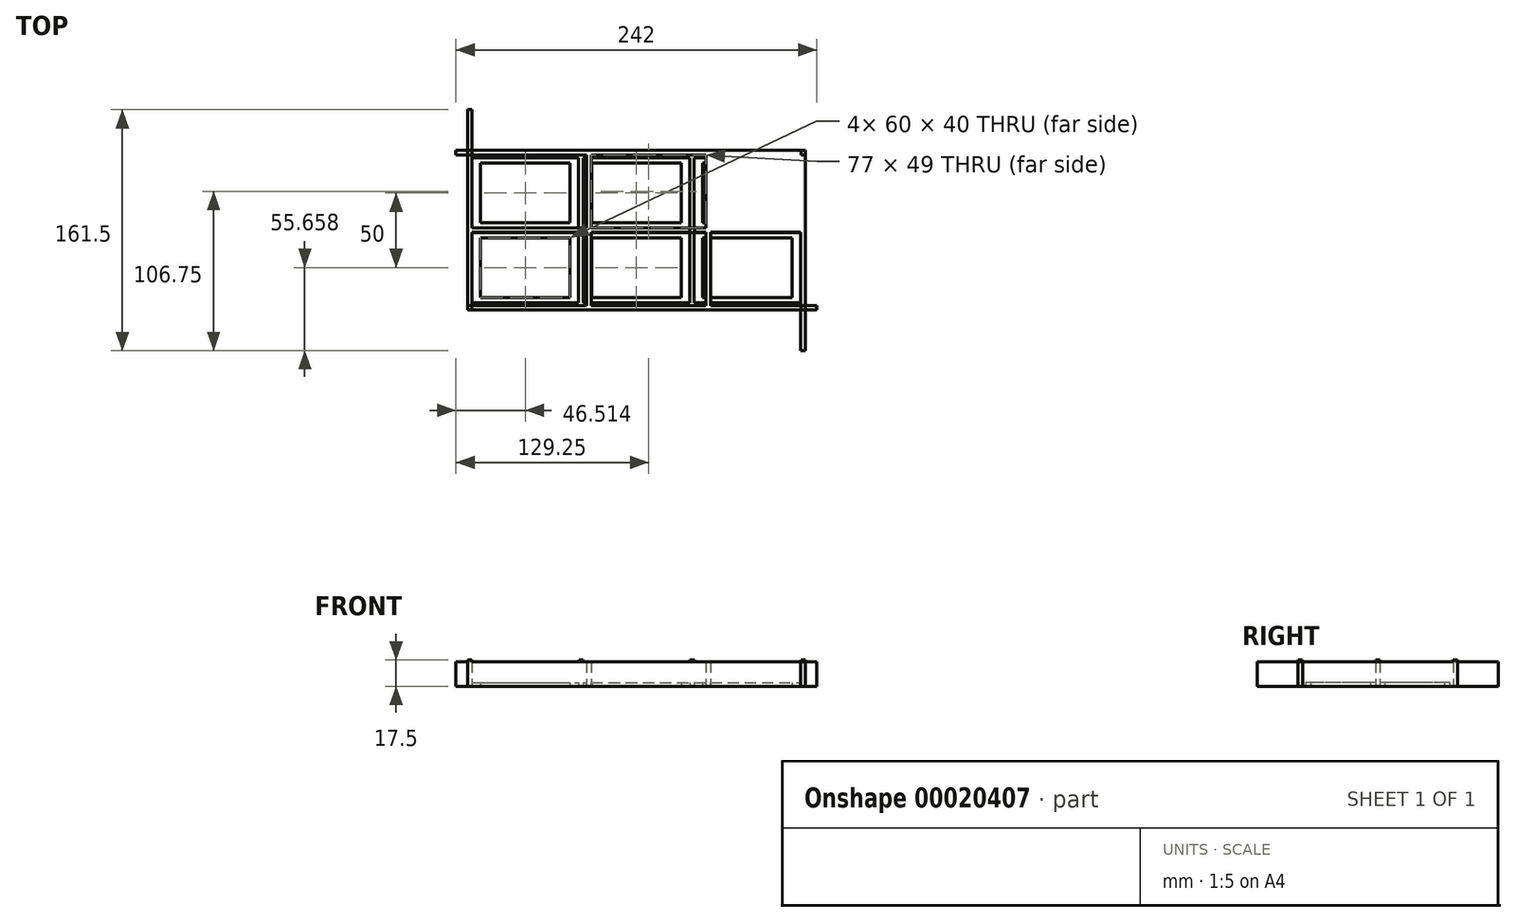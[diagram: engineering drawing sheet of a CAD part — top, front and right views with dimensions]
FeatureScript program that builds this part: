
annotation { "Feature Type Name" : "Feature", "Feature Type Description" : "" }
export const myFeature = defineFeature(function(context is Context, id is Id, definition is map)
    precondition{}
    {
        {
            var Q0;
            Q0=qCreatedBy(makeId("Top.planeOp"),FACE);
            var sketch = newSketch(context, id + "F0", { "sketchPlane" : qUnion([Q0])});
            skLineSegment(sketch, "E0.rect.bottom", {"start": v(113.25, 53.5) * mm, "end": v(-113.25, 53.5) * mm});
            skLineSegment(sketch, "E0.rect.top", {"start": v(113.25, -53.5) * mm, "end": v(-113.25, -53.5) * mm});
            skLineSegment(sketch, "E0.rect.left", {"start": v(113.25, 53.5) * mm, "end": v(113.25, -53.5) * mm});
            skLineSegment(sketch, "E0.rect.right", {"start": v(-113.25, 53.5) * mm, "end": v(-113.25, -53.5) * mm});
            skPoint(sketch, "E0.rect.middle", {"position": v(0, 0) * mm});
            skLineSegment(sketch, "E1.bottom", {"start": v(-110.25, 50.5) * mm, "end": v(-33.25, 50.5) * mm});
            skLineSegment(sketch, "E1.top", {"start": v(-110.25, 1.5) * mm, "end": v(-33.25, 1.5) * mm});
            skLineSegment(sketch, "E1.left", {"start": v(-110.25, 50.5) * mm, "end": v(-110.25, 1.5) * mm});
            skLineSegment(sketch, "E1.right", {"start": v(-33.25, 50.5) * mm, "end": v(-33.25, 1.5) * mm});
            skLineSegment(sketch, "E2.bottom", {"start": v(-110.25, -1.5) * mm, "end": v(-33.25, -1.5) * mm});
            skLineSegment(sketch, "E2.top", {"start": v(-110.25, -50.5) * mm, "end": v(-33.25, -50.5) * mm});
            skLineSegment(sketch, "E2.left", {"start": v(-110.25, -1.5) * mm, "end": v(-110.25, -50.5) * mm});
            skLineSegment(sketch, "E2.right", {"start": v(-33.25, -1.5) * mm, "end": v(-33.25, -50.5) * mm});
            skLineSegment(sketch, "E3.bottom", {"start": v(-30.25, 50.5) * mm, "end": v(46.75, 50.5) * mm});
            skLineSegment(sketch, "E3.top", {"start": v(-30.25, 1.5) * mm, "end": v(46.75, 1.5) * mm});
            skLineSegment(sketch, "E3.left", {"start": v(-30.25, 50.5) * mm, "end": v(-30.25, 1.5) * mm});
            skLineSegment(sketch, "E3.right", {"start": v(46.75, 50.5) * mm, "end": v(46.75, 1.5) * mm});
            skLineSegment(sketch, "E4.bottom", {"start": v(-30.25, -1.5) * mm, "end": v(46.75, -1.5) * mm});
            skLineSegment(sketch, "E4.top", {"start": v(-30.25, -50.5) * mm, "end": v(46.75, -50.5) * mm});
            skLineSegment(sketch, "E4.left", {"start": v(-30.25, -1.5) * mm, "end": v(-30.25, -50.5) * mm});
            skLineSegment(sketch, "E4.right", {"start": v(46.75, -1.5) * mm, "end": v(46.75, -50.5) * mm});
            skLineSegment(sketch, "E5.bottom", {"start": v(49.75, -1.5) * mm, "end": v(110.25, -1.5) * mm});
            skLineSegment(sketch, "E5.top", {"start": v(49.75, -50.5) * mm, "end": v(110.25, -50.5) * mm});
            skLineSegment(sketch, "E5.left", {"start": v(49.75, -1.5) * mm, "end": v(49.75, -50.5) * mm});
            skLineSegment(sketch, "E5.right", {"start": v(110.25, -1.5) * mm, "end": v(110.25, -50.5) * mm});
            skLineSegment(sketch, "E6.bottom", {"start": v(113.25, -50.5) * mm, "end": v(121, -50.5) * mm});
            skLineSegment(sketch, "E6.top", {"start": v(113.25, -53.5) * mm, "end": v(121, -53.5) * mm});
            skLineSegment(sketch, "E6.left", {"start": v(113.25, -50.5) * mm, "end": v(113.25, -53.5) * mm});
            skLineSegment(sketch, "E6.right", {"start": v(121, -50.5) * mm, "end": v(121, -53.5) * mm});
            skLineSegment(sketch, "E7.bottom", {"start": v(110.25, -53.5) * mm, "end": v(113.25, -53.5) * mm});
            skLineSegment(sketch, "E7.top", {"start": v(110.25, -80.75) * mm, "end": v(113.25, -80.75) * mm});
            skLineSegment(sketch, "E7.left", {"start": v(110.25, -53.5) * mm, "end": v(110.25, -80.75) * mm});
            skLineSegment(sketch, "E7.right", {"start": v(113.25, -53.5) * mm, "end": v(113.25, -80.75) * mm});
            skLineSegment(sketch, "E8.bottom", {"start": v(-110.25, 53.5) * mm, "end": v(-113.25, 53.5) * mm});
            skLineSegment(sketch, "E8.top", {"start": v(-110.25, 80.75) * mm, "end": v(-113.25, 80.75) * mm});
            skLineSegment(sketch, "E8.left", {"start": v(-110.25, 53.5) * mm, "end": v(-110.25, 80.75) * mm});
            skLineSegment(sketch, "E8.right", {"start": v(-113.25, 53.5) * mm, "end": v(-113.25, 80.75) * mm});
            skLineSegment(sketch, "E9.bottom", {"start": v(-113.25, 50.5) * mm, "end": v(-121, 50.5) * mm});
            skLineSegment(sketch, "E9.top", {"start": v(-113.25, 53.5) * mm, "end": v(-121, 53.5) * mm});
            skLineSegment(sketch, "E9.left", {"start": v(-113.25, 50.5) * mm, "end": v(-113.25, 53.5) * mm});
            skLineSegment(sketch, "E9.right", {"start": v(-121, 50.5) * mm, "end": v(-121, 53.5) * mm});
            skPoint(sketch, "E10.left.start.orphan", {"position": v(49.75, 50.5) * mm});
            skPoint(sketch, "E10.top.start.orphan", {"position": v(49.75, 1.5) * mm});
            skPoint(sketch, "E10.right.end.orphan", {"position": v(110.25, 1.5) * mm});
            skSolve(sketch);
        }
        {
            var Q0;
            Q0=qSketchRegion(id+"F0",true);
            extrude(context, id + "F1", {"entities" : qUnion([Q0]), "depth" : 16.5 * mm});
        }
        {
            var Q0;
            Q0=qCreatedBy(makeId("Top.planeOp"),FACE);
            var sketch = newSketch(context, id + "F2", { "sketchPlane" : qUnion([Q0])});
            skPoint(sketch, "E11.rect.middle", {"position": v(0.01, -0.1) * mm});
            skLineSegment(sketch, "E12.bottom", {"start": v(-110.24, 48.4) * mm, "end": v(-38.74, 48.4) * mm});
            skLineSegment(sketch, "E12.top", {"start": v(-110.24, 1.4) * mm, "end": v(-38.74, 1.4) * mm});
            skLineSegment(sketch, "E12.left", {"start": v(-110.24, 48.4) * mm, "end": v(-110.24, 1.4) * mm});
            skLineSegment(sketch, "E12.right", {"start": v(-38.74, 48.4) * mm, "end": v(-38.74, 1.4) * mm});
            skLineSegment(sketch, "E13.bottom", {"start": v(-110.24, -1.6) * mm, "end": v(-38.74, -1.6) * mm});
            skLineSegment(sketch, "E13.top", {"start": v(-110.24, -48.6) * mm, "end": v(-38.74, -48.6) * mm});
            skLineSegment(sketch, "E13.left", {"start": v(-110.24, -1.6) * mm, "end": v(-110.24, -48.6) * mm});
            skLineSegment(sketch, "E13.right", {"start": v(-38.74, -1.6) * mm, "end": v(-38.74, -48.6) * mm});
            skLineSegment(sketch, "E14.bottom", {"start": v(-35.74, 48.4) * mm, "end": v(35.76, 48.4) * mm});
            skLineSegment(sketch, "E14.top", {"start": v(-35.74, 1.4) * mm, "end": v(35.76, 1.4) * mm});
            skLineSegment(sketch, "E14.left", {"start": v(-35.74, 48.4) * mm, "end": v(-35.74, 1.4) * mm});
            skLineSegment(sketch, "E14.right", {"start": v(35.76, 48.4) * mm, "end": v(35.76, 1.4) * mm});
            skLineSegment(sketch, "E15.bottom", {"start": v(-35.74, -1.6) * mm, "end": v(35.76, -1.6) * mm});
            skLineSegment(sketch, "E15.top", {"start": v(-35.74, -48.6) * mm, "end": v(35.76, -48.6) * mm});
            skLineSegment(sketch, "E15.left", {"start": v(-35.74, -1.6) * mm, "end": v(-35.74, -48.6) * mm});
            skLineSegment(sketch, "E15.right", {"start": v(35.76, -1.6) * mm, "end": v(35.76, -48.6) * mm});
            skLineSegment(sketch, "E16.bottom", {"start": v(38.76, 48.4) * mm, "end": v(110.26, 48.4) * mm});
            skLineSegment(sketch, "E16.top", {"start": v(38.76, 1.4) * mm, "end": v(110.26, 1.4) * mm});
            skLineSegment(sketch, "E16.left", {"start": v(38.76, 48.4) * mm, "end": v(38.76, 1.4) * mm});
            skLineSegment(sketch, "E16.right", {"start": v(110.26, 48.4) * mm, "end": v(110.26, 1.4) * mm});
            skLineSegment(sketch, "E17.bottom", {"start": v(38.76, -1.6) * mm, "end": v(110.26, -1.6) * mm});
            skLineSegment(sketch, "E17.top", {"start": v(38.76, -48.6) * mm, "end": v(110.26, -48.6) * mm});
            skLineSegment(sketch, "E17.left", {"start": v(38.76, -1.6) * mm, "end": v(38.76, -48.6) * mm});
            skLineSegment(sketch, "E17.right", {"start": v(110.26, -1.6) * mm, "end": v(110.26, -48.6) * mm});
            skLineSegment(sketch, "E18.bottom", {"start": v(-104.49, 44.9) * mm, "end": v(-44.49, 44.9) * mm});
            skLineSegment(sketch, "E18.top", {"start": v(-104.49, 4.9) * mm, "end": v(-44.49, 4.9) * mm});
            skLineSegment(sketch, "E18.left", {"start": v(-104.49, 44.9) * mm, "end": v(-104.49, 4.9) * mm});
            skLineSegment(sketch, "E18.right", {"start": v(-44.49, 44.9) * mm, "end": v(-44.49, 4.9) * mm});
            skLineSegment(sketch, "E19.bottom", {"start": v(-104.49, -5.1) * mm, "end": v(-44.49, -5.1) * mm});
            skLineSegment(sketch, "E19.top", {"start": v(-104.49, -45.1) * mm, "end": v(-44.49, -45.1) * mm});
            skLineSegment(sketch, "E19.left", {"start": v(-104.49, -5.1) * mm, "end": v(-104.49, -45.1) * mm});
            skLineSegment(sketch, "E19.right", {"start": v(-44.49, -5.1) * mm, "end": v(-44.49, -45.1) * mm});
            skLineSegment(sketch, "E20.bottom", {"start": v(-29.99, 44.9) * mm, "end": v(30.01, 44.9) * mm});
            skLineSegment(sketch, "E20.top", {"start": v(-29.99, 4.9) * mm, "end": v(30.01, 4.9) * mm});
            skLineSegment(sketch, "E20.left", {"start": v(-29.99, 44.9) * mm, "end": v(-29.99, 4.9) * mm});
            skLineSegment(sketch, "E20.right", {"start": v(30.01, 44.9) * mm, "end": v(30.01, 4.9) * mm});
            skLineSegment(sketch, "E21.bottom", {"start": v(-29.99, -5.1) * mm, "end": v(30.01, -5.1) * mm});
            skLineSegment(sketch, "E21.top", {"start": v(-29.99, -45.1) * mm, "end": v(30.01, -45.1) * mm});
            skLineSegment(sketch, "E21.left", {"start": v(-29.99, -5.1) * mm, "end": v(-29.99, -45.1) * mm});
            skLineSegment(sketch, "E21.right", {"start": v(30.01, -5.1) * mm, "end": v(30.01, -45.1) * mm});
            skLineSegment(sketch, "E22.bottom", {"start": v(44.51, 44.9) * mm, "end": v(104.51, 44.9) * mm});
            skLineSegment(sketch, "E22.top", {"start": v(44.51, 4.9) * mm, "end": v(104.51, 4.9) * mm});
            skLineSegment(sketch, "E22.left", {"start": v(44.51, 44.9) * mm, "end": v(44.51, 4.9) * mm});
            skLineSegment(sketch, "E22.right", {"start": v(104.51, 44.9) * mm, "end": v(104.51, 4.9) * mm});
            skLineSegment(sketch, "E23.bottom", {"start": v(44.51, -5.1) * mm, "end": v(104.51, -5.1) * mm});
            skLineSegment(sketch, "E23.top", {"start": v(44.51, -45.1) * mm, "end": v(104.51, -45.1) * mm});
            skLineSegment(sketch, "E23.left", {"start": v(44.51, -5.1) * mm, "end": v(44.51, -45.1) * mm});
            skLineSegment(sketch, "E23.right", {"start": v(104.51, -5.1) * mm, "end": v(104.51, -45.1) * mm});
            skSolve(sketch);
        }
        {
            var Q0;
            Q0=qSketchRegion(id+"F2",true);
            extrude(context, id + "F3", {"entities" : qUnion([Q0]), "operationType" : NewBodyOperationType.ADD, "depth" : 2.5 * mm});
        }
        {
            var Q0;
            Q0=makeQuery(id+"F1.opExtrude","CAP_FACE",FACE,{"disambiguationData":[OSD([sQuery(id+"F0.wireOp",EDGE,"E0.rect.bottom"),sQuery(id+"F0.wireOp",EDGE,"E0.rect.top"),sQuery(id+"F0.wireOp",EDGE,"E0.rect.left"),sQuery(id+"F0.wireOp",EDGE,"E0.rect.right"),sQuery(id+"F0.wireOp",EDGE,"E1.bottom"),sQuery(id+"F0.wireOp",EDGE,"E1.top"),sQuery(id+"F0.wireOp",EDGE,"E1.left"),sQuery(id+"F0.wireOp",EDGE,"E1.right"),sQuery(id+"F0.wireOp",EDGE,"E2.bottom"),sQuery(id+"F0.wireOp",EDGE,"E2.top"),sQuery(id+"F0.wireOp",EDGE,"E2.left"),sQuery(id+"F0.wireOp",EDGE,"E2.right"),sQuery(id+"F0.wireOp",EDGE,"E3.bottom"),sQuery(id+"F0.wireOp",EDGE,"E3.top"),sQuery(id+"F0.wireOp",EDGE,"E3.left"),sQuery(id+"F0.wireOp",EDGE,"E3.right"),sQuery(id+"F0.wireOp",EDGE,"E4.bottom"),sQuery(id+"F0.wireOp",EDGE,"E4.top"),sQuery(id+"F0.wireOp",EDGE,"E4.left"),sQuery(id+"F0.wireOp",EDGE,"E4.right"),sQuery(id+"F0.wireOp",EDGE,"E10.bottom"),sQuery(id+"F0.wireOp",EDGE,"E10.top"),sQuery(id+"F0.wireOp",EDGE,"E10.left"),sQuery(id+"F0.wireOp",EDGE,"E10.right"),sQuery(id+"F0.wireOp",EDGE,"E5.bottom"),sQuery(id+"F0.wireOp",EDGE,"E5.top"),sQuery(id+"F0.wireOp",EDGE,"E5.left"),sQuery(id+"F0.wireOp",EDGE,"E5.right"),sQuery(id+"F0.wireOp",EDGE,"E6.bottom"),sQuery(id+"F0.wireOp",EDGE,"E6.top"),sQuery(id+"F0.wireOp",EDGE,"E6.right"),sQuery(id+"F0.wireOp",EDGE,"E7.top"),sQuery(id+"F0.wireOp",EDGE,"E7.left"),sQuery(id+"F0.wireOp",EDGE,"E7.right"),sQuery(id+"F0.wireOp",EDGE,"E8.top"),sQuery(id+"F0.wireOp",EDGE,"E8.left"),sQuery(id+"F0.wireOp",EDGE,"E8.right"),sQuery(id+"F0.wireOp",EDGE,"E9.bottom"),sQuery(id+"F0.wireOp",EDGE,"E9.top"),sQuery(id+"F0.wireOp",EDGE,"E9.right")])],"isStart":false});
            var sketch = newSketch(context, id + "F4", { "sketchPlane" : qUnion([Q0])});
            skPoint(sketch, "E24.rect.middle", {"position": v(0.15, -0.13) * mm});
            skLineSegment(sketch, "E25.bottom", {"start": v(-110.1, 50.37) * mm, "end": v(-113.25, 50.37) * mm});
            skLineSegment(sketch, "E25.top", {"start": v(-110.1, 53.5) * mm, "end": v(-113.25, 53.5) * mm});
            skLineSegment(sketch, "E25.left", {"start": v(-110.1, 50.37) * mm, "end": v(-110.1, 53.5) * mm});
            skLineSegment(sketch, "E25.right", {"start": v(-113.25, 50.37) * mm, "end": v(-113.25, 53.5) * mm});
            skLineSegment(sketch, "E26.bottom", {"start": v(-110.1, -50.63) * mm, "end": v(-113.25, -50.63) * mm});
            skLineSegment(sketch, "E26.top", {"start": v(-110.1, -53.5) * mm, "end": v(-113.25, -53.5) * mm});
            skLineSegment(sketch, "E26.left", {"start": v(-110.1, -50.63) * mm, "end": v(-110.1, -53.5) * mm});
            skLineSegment(sketch, "E26.right", {"start": v(-113.25, -50.63) * mm, "end": v(-113.25, -53.5) * mm});
            skLineSegment(sketch, "E27.bottom", {"start": v(-38.6, -1.63) * mm, "end": v(-35.6, -1.63) * mm});
            skLineSegment(sketch, "E27.top", {"start": v(-38.6, 1.37) * mm, "end": v(-35.6, 1.37) * mm});
            skLineSegment(sketch, "E27.left", {"start": v(-38.6, -1.63) * mm, "end": v(-38.6, 1.37) * mm});
            skLineSegment(sketch, "E27.right", {"start": v(-35.6, -1.63) * mm, "end": v(-35.6, 1.37) * mm});
            skLineSegment(sketch, "E28.bottom", {"start": v(110.4, -50.63) * mm, "end": v(113.25, -50.63) * mm});
            skLineSegment(sketch, "E28.top", {"start": v(110.4, -53.5) * mm, "end": v(113.25, -53.5) * mm});
            skLineSegment(sketch, "E28.left", {"start": v(110.4, -50.63) * mm, "end": v(110.4, -53.5) * mm});
            skLineSegment(sketch, "E28.right", {"start": v(113.25, -50.63) * mm, "end": v(113.25, -53.5) * mm});
            skLineSegment(sketch, "E29.bottom", {"start": v(110.4, 50.37) * mm, "end": v(113.25, 50.37) * mm});
            skLineSegment(sketch, "E29.top", {"start": v(110.4, 53.5) * mm, "end": v(113.25, 53.5) * mm});
            skLineSegment(sketch, "E29.left", {"start": v(110.4, 50.37) * mm, "end": v(110.4, 53.5) * mm});
            skLineSegment(sketch, "E29.right", {"start": v(113.25, 50.37) * mm, "end": v(113.25, 53.5) * mm});
            skLineSegment(sketch, "E30.bottom", {"start": v(35.9, 1.37) * mm, "end": v(38.9, 1.37) * mm});
            skLineSegment(sketch, "E30.top", {"start": v(35.9, -1.63) * mm, "end": v(38.9, -1.63) * mm});
            skLineSegment(sketch, "E30.left", {"start": v(35.9, 1.37) * mm, "end": v(35.9, -1.63) * mm});
            skLineSegment(sketch, "E30.right", {"start": v(38.9, 1.37) * mm, "end": v(38.9, -1.63) * mm});
            skSolve(sketch);
        }
        {
            var Q0;
            Q0=qSketchRegion(id+"F4",true);
            extrude(context, id + "F5", {"entities" : qUnion([Q0]), "operationType" : NewBodyOperationType.ADD, "depth" : 1 * mm});
        }
    });
